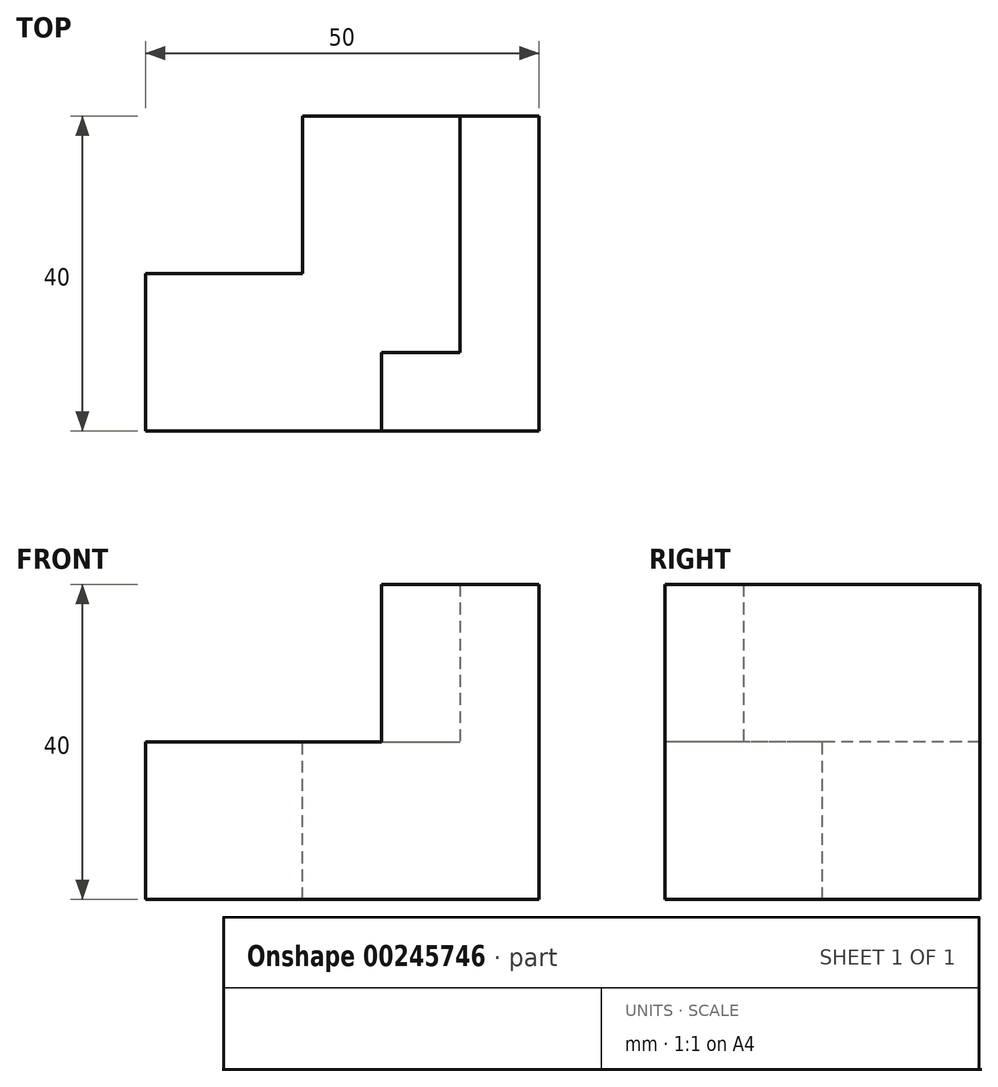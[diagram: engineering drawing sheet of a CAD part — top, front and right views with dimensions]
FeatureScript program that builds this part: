
annotation { "Feature Type Name" : "Feature", "Feature Type Description" : "" }
export const myFeature = defineFeature(function(context is Context, id is Id, definition is map)
    precondition{}
    {
        {
            var Q0;
            Q0=qCreatedBy(makeId("Right.planeOp"),FACE);
            var sketch = newSketch(context, id + "F0", { "sketchPlane" : qUnion([Q0])});
            skLineSegment(sketch, "E0", {"start": v(0, 0) * mm, "end": v(0, 40) * mm});
            skLineSegment(sketch, "E1", {"start": v(0, 0) * mm, "end": v(40, 0) * mm});
            skLineSegment(sketch, "E2", {"start": v(40, 0) * mm, "end": v(40, 40) * mm});
            skLineSegment(sketch, "E3", {"start": v(0, 40) * mm, "end": v(40, 40) * mm});
            skSolve(sketch);
        }
        {
            var Q0;
            Q0 = qSketchRegion(id + "F0", true);
            extrude(context, id + "F1", {"entities" : qUnion([Q0]), "oppositeDirection" : true, "depth" : 10 * mm});
        }
        {
            var Q0;
            Q0=makeQuery(id+"F1.opExtrude","CAP_FACE",FACE,{"disambiguationData":[OSD([sQuery(id+"F0.wireOp",EDGE,"E0"),sQuery(id+"F0.wireOp",EDGE,"E1"),sQuery(id+"F0.wireOp",EDGE,"E2"),sQuery(id+"F0.wireOp",EDGE,"E3")])],"isStart":false});
            var sketch = newSketch(context, id + "F2", { "sketchPlane" : qUnion([Q0])});
            skLineSegment(sketch, "E4", {"start": v(-40, 0) * mm, "end": v(-40, 20) * mm});
            skLineSegment(sketch, "E5", {"start": v(-40, 20) * mm, "end": v(0, 20) * mm});
            skLineSegment(sketch, "E6", {"start": v(0, 20) * mm, "end": v(0, 0) * mm});
            skLineSegment(sketch, "E7", {"start": v(0, 0) * mm, "end": v(-40, 0) * mm});
            skSolve(sketch);
        }
        {
            var Q0;
            Q0=makeQuery(id+"F2.imprint","IMPRINT",FACE,{"disambiguationData":[TD([[makeQuery(id+"F2.imprint","IMPRINT",EDGE,{"derivedFrom":sQuery(id+"F2.wireOp",EDGE,"E4")}),-1.0]])]});
            extrude(context, id + "F3", {"entities" : qUnion([Q0]), "operationType" : NewBodyOperationType.ADD, "depth" : 20 * mm});
        }
        {
            var Q0;
            Q0=makeQuery(id+"F3.opExtrude","CAP_FACE",FACE,{"disambiguationData":[OSD([sQuery(id+"F2.wireOp",EDGE,"E4"),sQuery(id+"F2.wireOp",EDGE,"E5"),sQuery(id+"F2.wireOp",EDGE,"E6"),sQuery(id+"F2.wireOp",EDGE,"E7")])],"isStart":false});
            var sketch = newSketch(context, id + "F4", { "sketchPlane" : qUnion([Q0])});
            skLineSegment(sketch, "E8", {"start": v(-20, 0) * mm, "end": v(-20, 20) * mm});
            skLineSegment(sketch, "E9", {"start": v(-20, 20) * mm, "end": v(0, 20) * mm});
            skLineSegment(sketch, "E10", {"start": v(0, 20) * mm, "end": v(0, 0) * mm});
            skLineSegment(sketch, "E11", {"start": v(0, 0) * mm, "end": v(-20, 0) * mm});
            skSolve(sketch);
        }
        {
            var Q0;
            Q0=makeQuery(id+"F4.imprint","IMPRINT",FACE,{"disambiguationData":[TD([[makeQuery(id+"F4.imprint","IMPRINT",EDGE,{"derivedFrom":sQuery(id+"F4.wireOp",EDGE,"E8")}),-1.0]])]});
            extrude(context, id + "F5", {"entities" : qUnion([Q0]), "operationType" : NewBodyOperationType.ADD, "depth" : 20 * mm});
        }
        {
            var Q0;
            Q0=makeQuery(id+"F1.opExtrude","CAP_FACE",FACE,{"disambiguationData":[OSD([sQuery(id+"F0.wireOp",EDGE,"E0"),sQuery(id+"F0.wireOp",EDGE,"E1"),sQuery(id+"F0.wireOp",EDGE,"E2"),sQuery(id+"F0.wireOp",EDGE,"E3")])],"isStart":false});
            var sketch = newSketch(context, id + "F6", { "sketchPlane" : qUnion([Q0])});
            skLineSegment(sketch, "E12", {"start": v(0, 40) * mm, "end": v(-10, 40) * mm});
            skLineSegment(sketch, "E13", {"start": v(-10, 40) * mm, "end": v(-10, 20) * mm});
            skLineSegment(sketch, "E14", {"start": v(-10, 20) * mm, "end": v(0, 20) * mm});
            skLineSegment(sketch, "E15", {"start": v(0, 20) * mm, "end": v(0, 40) * mm});
            skSolve(sketch);
        }
        {
            var Q0;
            Q0=makeQuery(id+"F6.imprint","IMPRINT",FACE,{"disambiguationData":[TD([[makeQuery(id+"F6.imprint","IMPRINT",EDGE,{"derivedFrom":sQuery(id+"F6.wireOp",EDGE,"E12")}),1.0]])]});
            extrude(context, id + "F7", {"entities" : qUnion([Q0]), "operationType" : NewBodyOperationType.ADD, "depth" : 10 * mm});
        }
    });
